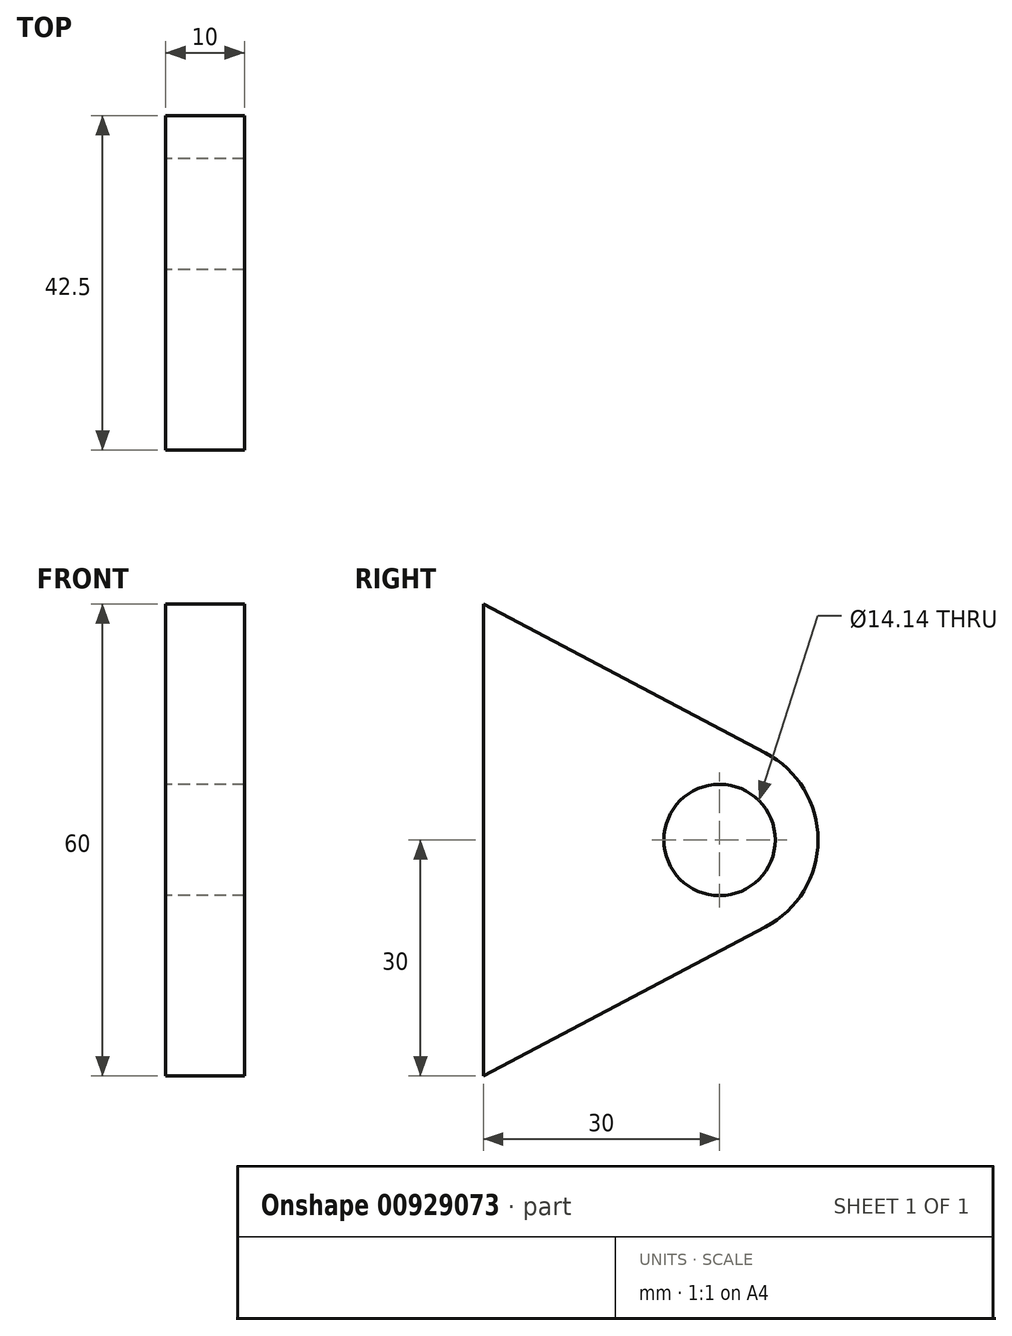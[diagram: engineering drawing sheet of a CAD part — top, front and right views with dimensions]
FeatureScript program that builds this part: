
annotation { "Feature Type Name" : "Feature", "Feature Type Description" : "" }
export const myFeature = defineFeature(function(context is Context, id is Id, definition is map)
    precondition{}
    {
        {
            var Q0;
            Q0=qCreatedBy(makeId("Right.planeOp"),FACE);
            var sketch = newSketch(context, id + "F0", { "sketchPlane" : qUnion([Q0])});
            skLineSegment(sketch, "E0", {"start": v(0, 0) * mm, "end": v(0, 60) * mm});
            skLineSegment(sketch, "E1", {"start": v(0, 60) * mm, "end": v(35.84, 41.05) * mm});
            skLineSegment(sketch, "E2", {"start": v(0, 0) * mm, "end": v(35.84, 18.95) * mm});
            skArc(sketch, "E3", {"start": v(35.84, 18.95) * mm, "mid": v(42.5, 30) * mm, "end": v(35.84, 41.05) * mm});
            skCircle(sketch, "E4", {"center": v(30, 30) * mm, "radius": 7.07 * mm});
            skSolve(sketch);
        }
        {
            var Q0;
            Q0 = qSketchRegion(id + "F0", true);
            extrude(context, id + "F1", {"entities" : qUnion([Q0]), "depth" : 10 * mm, "offsetDistance" : 25 * mm});
        }
    });
